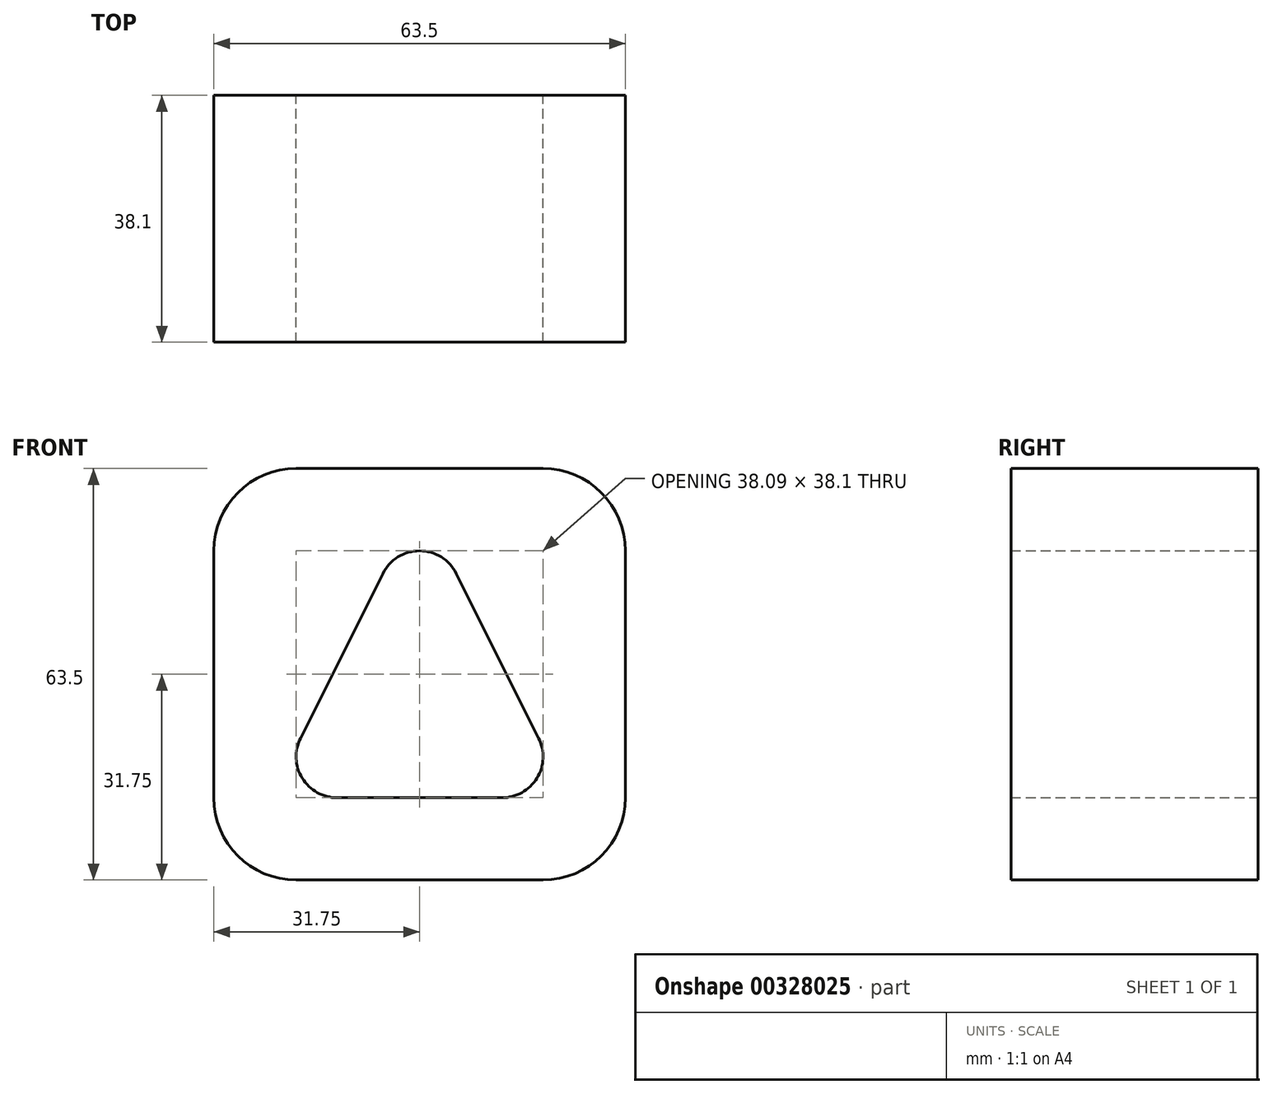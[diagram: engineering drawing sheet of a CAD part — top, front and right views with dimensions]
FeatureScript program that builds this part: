
annotation { "Feature Type Name" : "Feature", "Feature Type Description" : "" }
export const myFeature = defineFeature(function(context is Context, id is Id, definition is map)
    precondition{}
    {
        {
            var Q0;
            Q0=qCreatedBy(makeId("Front.planeOp"),FACE);
            var sketch = newSketch(context, id + "F0", { "sketchPlane" : qUnion([Q0])});
            skLineSegment(sketch, "E0", {"start": v(0, 0) * mm, "end": v(63.5, 0) * mm});
            skLineSegment(sketch, "E1", {"start": v(63.5, 0) * mm, "end": v(63.5, 63.5) * mm});
            skLineSegment(sketch, "E2", {"start": v(63.5, 63.5) * mm, "end": v(0, 63.5) * mm});
            skLineSegment(sketch, "E3", {"start": v(0, 63.5) * mm, "end": v(0, 0) * mm});
            skArc(sketch, "E4", {"start": v(13.37, 21.89) * mm, "mid": v(13.65, 15.71) * mm, "end": v(19.05, 12.7) * mm});
            skArc(sketch, "E5", {"start": v(37.43, 47.29) * mm, "mid": v(31.75, 50.8) * mm, "end": v(26.07, 47.29) * mm});
            skArc(sketch, "E6", {"start": v(44.45, 12.7) * mm, "mid": v(49.85, 15.71) * mm, "end": v(50.13, 21.89) * mm});
            skLineSegment(sketch, "E7", {"start": v(37.43, 47.29) * mm, "end": v(50.13, 21.89) * mm});
            skLineSegment(sketch, "E8", {"start": v(44.45, 12.7) * mm, "end": v(19.05, 12.7) * mm});
            skLineSegment(sketch, "E9", {"start": v(13.37, 21.89) * mm, "end": v(26.07, 47.29) * mm});
            skSolve(sketch);
        }
        {
            var Q0;
            Q0=makeQuery(id+"F0.imprint","IMPRINT",FACE,{"disambiguationData":[TD([[makeQuery(id+"F0.imprint","IMPRINT",EDGE,{"derivedFrom":sQuery(id+"F0.wireOp",EDGE,"E0")}),1.0]])]});
            extrude(context, id + "F1", {"entities" : qUnion([Q0]), "depth" : 38.1 * mm});
        }
        {
            var Q0;
            Q0=makeQuery(id+"F1.opExtrude","SWEPT_EDGE",EDGE,{"disambiguationData":[OSD([sQuery(id+"F0.wireOp",EDGE,"E0"),sQuery(id+"F0.wireOp",EDGE,"E1")])]});
            var Q1;
            Q1=makeQuery(id+"F1.opExtrude","SWEPT_EDGE",EDGE,{"disambiguationData":[OSD([sQuery(id+"F0.wireOp",EDGE,"E1"),sQuery(id+"F0.wireOp",EDGE,"E2")])]});
            var Q2;
            Q2=makeQuery(id+"F1.opExtrude","SWEPT_EDGE",EDGE,{"disambiguationData":[OSD([sQuery(id+"F0.wireOp",EDGE,"E2"),sQuery(id+"F0.wireOp",EDGE,"E3")])]});
            var Q3;
            Q3=makeQuery(id+"F1.opExtrude","SWEPT_EDGE",EDGE,{"disambiguationData":[OSD([sQuery(id+"F0.wireOp",EDGE,"E0"),sQuery(id+"F0.wireOp",EDGE,"E3")])]});
            fillet(context, id + "F2", {"entities" : qUnion([Q0, Q1, Q2, Q3]), "radius" : 12.7 * mm, "tangentPropagation" : true, "allowEdgeOverflow" : false});
        }
    });
